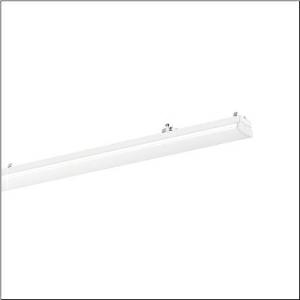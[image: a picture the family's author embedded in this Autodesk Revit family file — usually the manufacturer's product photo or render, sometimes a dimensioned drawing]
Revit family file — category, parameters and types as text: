
# Revit family: licross_21_recessed_opal_mo_52tl1dcn485g
name_source: partatom
category: Lighting Fixtures
units: mm (PartAtom-declared; Revit-internal decimal feet)

## family parameters
Cut with Voids When Loaded = No
Host = Face
Light Source = No
Part Type = Normal
Room Calculation Point = No
Round Connector Dimension = Use Diameter
Shared = No

## types (1)
- --- (1 x LED, 8780 lm, 49.9 W, 4000K)
    Apparent Load = 50 VA
    CIE Flux Codes = 44 73 91 87 100
    Color Rendering = 80
    Color Temperature = 4000K
    Default Elevation = 1800 mm
    Description = Licross 21 recessed opal MO, luminaire insert, of sheet steel, galvanised, coil coated, white, length: 1.500mm, width: 66mm, height: 67mm, LED rated luminous flux: 8.780lm, light colour: 840, SDCM (Standard Deviation of Colour Matching)MacAdam ≤ 3 SDCM (initial), control gear: ON/OFF Multilumen, CLOi, with plug, 3-pole, with phase selection, mains connection: 220..240V, AC, 50/60Hz, start of lifetime: 50W, end of service life: 61W, internal wiring halogen-free, primary optical cover: cover, of PMMA, light emission: direct with ceiling illumination distribution, primary light characteristic: symmetric, protection rating (complete): IP40, insulation class (complete): insulation class I (protective earthing), certification: CE, ENEC, VDE, UKCA, protection symbol: D if used in an environment without relevant dust loads with corresponding accessories, impact resistance: IK06, permissible ambient temperature for indoor applications: -35..+40°C, corresponds to IFS (International Featured Standards) requirements for safety and quality in the food industry, reducing of maximum allowable ambient temperature of 5°C with ceiling mounting, LABS conformity tested according to VDMA 24364:2018-05, The light source and the operating device comply with the requirements of the Ecodesign Regulation (EU) 2019/2020 and are replaceable in accordance with this regulation, packaging unit: 1 piece
    Height = 83 mm
    Lamp = 1 x LED
    Lamp Light Flux = 8780 lm
    Lamp Power = 49.9 W
    Lamp count = 1
    Length = 1500 mm
    Luminous efficacy = 176 lm/W
    Manufacturer = Siteco
    ModVariant = No
    Model = 52TL1DCN485G
    Mounting Place = Ceiling
    Mounting Type = Pendant
    Number of Poles = 1
    OnlyDefault = Yes
    Power Factor = 1
    Product Name = Licross 21 recessed opal MO
    Product group = luminaire insert | ceiling pendant
    ProductGroupID = 901
    Protection Class = Protection class I
    Protection Degree = IP 40
    RLX_Detail_Level = 1
    RLX_Emergency_Light_Flux = 0 lm
    RLX_Emergency_Type = 0
    RLX_Emergency_Type_DB = No
    RlxData = <blob elided: 25037 chars, md5=db89da96>
    Socket = socket
    Standby Power = 0 W
    System Light Flux = 8780 lm
    System Power = 50 W
    Type Comments = factory setting: luminous flux: 100 % | (A | C | E) | 116 mA
    Type Image = l_1313666.jpg
    URL = http://relux.com
    VarID = @adj_075959
    Voltage = 0 V
    Weight = 0.00 kg
    Width = 76 mm

## geometry (parser evidence)
native form markers: Blend x4, Sweep x14
no freeform markers — native parametric forms only
